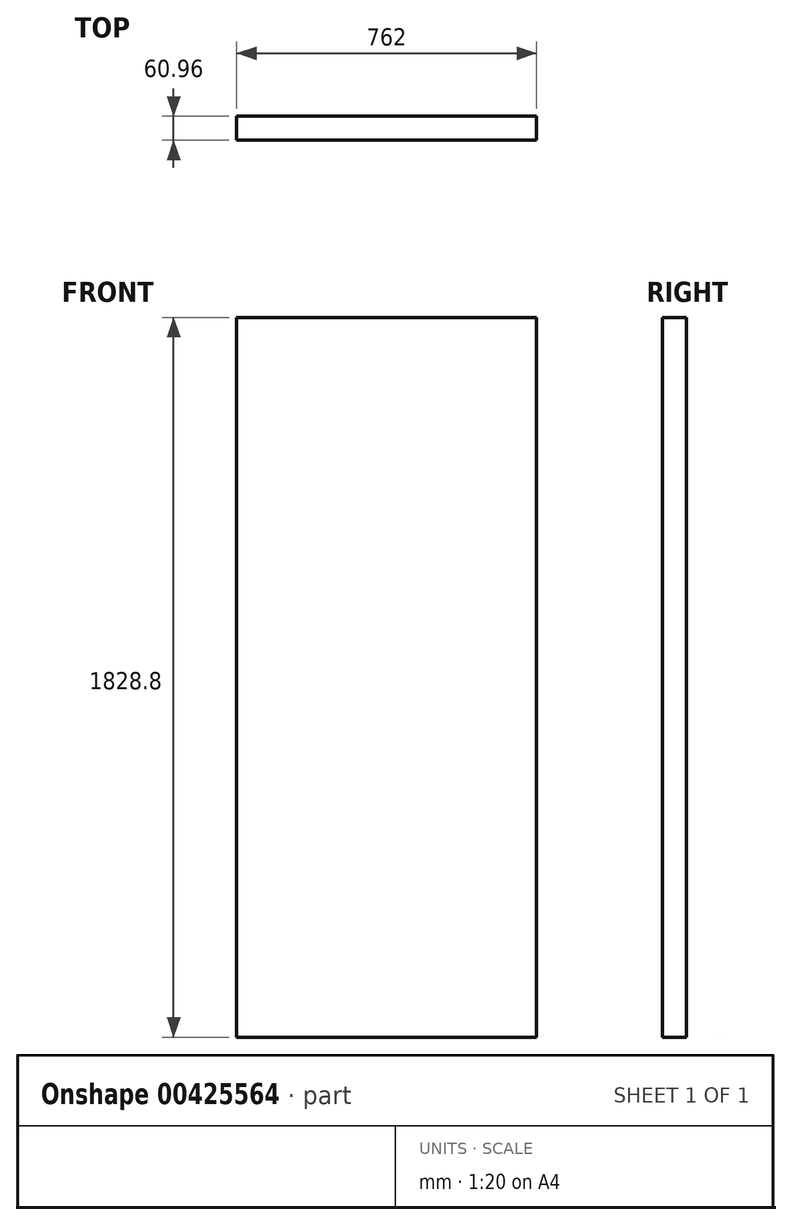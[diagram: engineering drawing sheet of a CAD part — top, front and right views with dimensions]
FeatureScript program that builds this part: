
annotation { "Feature Type Name" : "Feature", "Feature Type Description" : "" }
export const myFeature = defineFeature(function(context is Context, id is Id, definition is map)
    precondition{}
    {
        {
            var Q0;
            Q0=qCreatedBy(makeId("Front.planeOp"),FACE);
            var sketch = newSketch(context, id + "F0", { "sketchPlane" : qUnion([Q0])});
            skLineSegment(sketch, "E0.bottom", {"start": v(381, 914.4) * mm, "end": v(-381, 914.4) * mm});
            skLineSegment(sketch, "E0.top", {"start": v(381, -914.4) * mm, "end": v(-381, -914.4) * mm});
            skLineSegment(sketch, "E0.left", {"start": v(381, 914.4) * mm, "end": v(381, -914.4) * mm});
            skLineSegment(sketch, "E0.right", {"start": v(-381, 914.4) * mm, "end": v(-381, -914.4) * mm});
            skPoint(sketch, "E0.middle", {"position": v(0, 0) * mm});
            skSolve(sketch);
        }
        {
            var Q0;
            Q0 = qSketchRegion(id + "F0", true);
            extrude(context, id + "F1", {"entities" : qUnion([Q0]), "depth" : 60.96 * mm});
        }
    });
